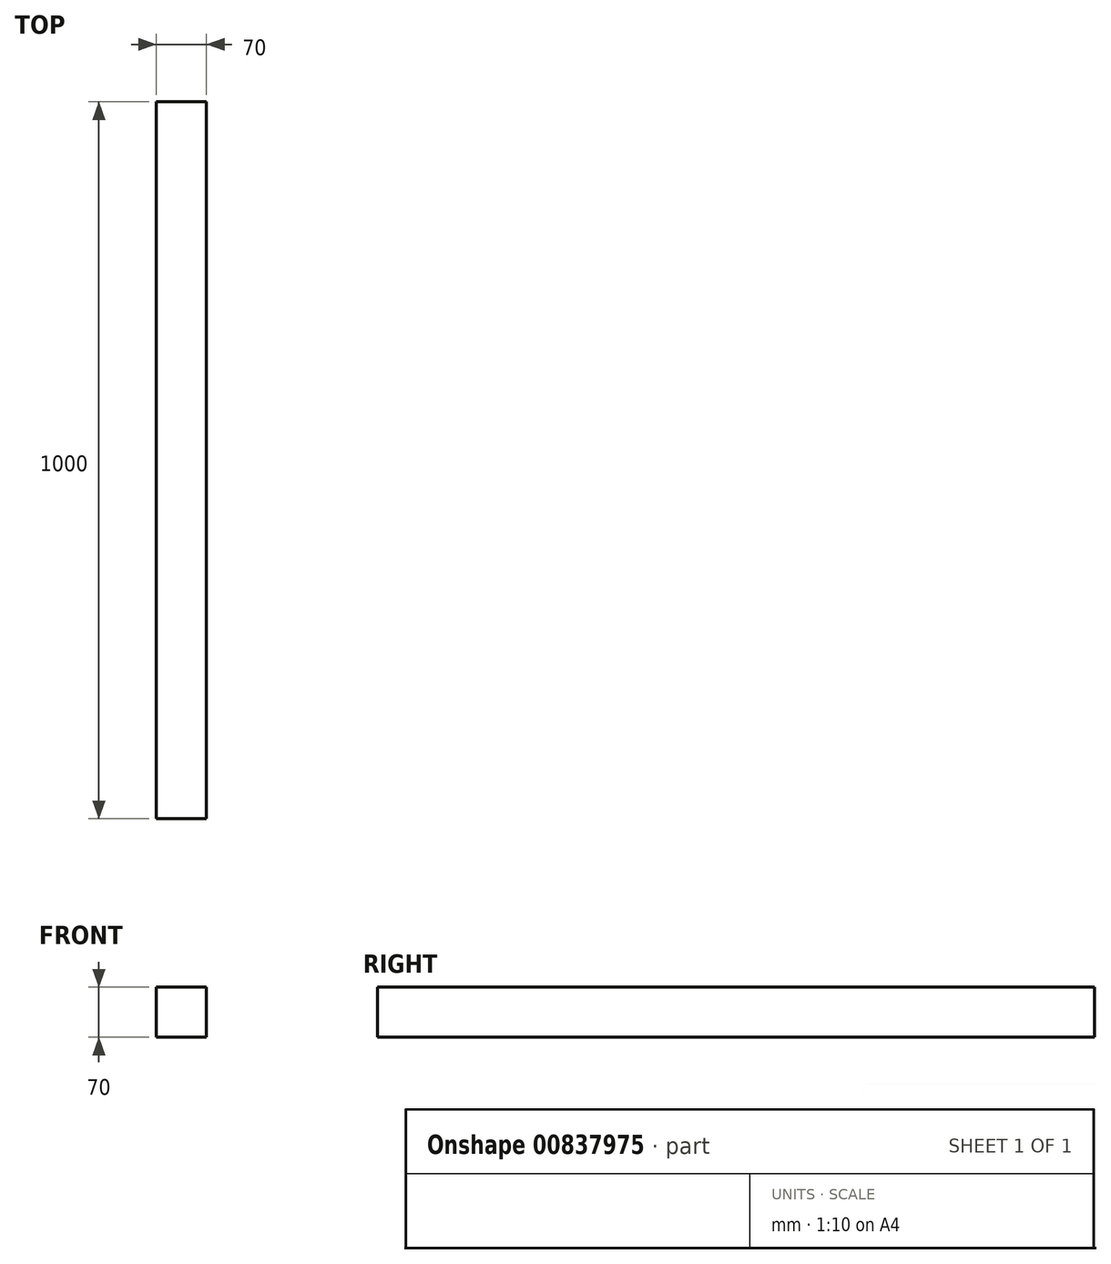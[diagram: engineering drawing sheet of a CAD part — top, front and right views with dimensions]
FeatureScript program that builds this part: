
annotation { "Feature Type Name" : "Feature", "Feature Type Description" : "" }
export const myFeature = defineFeature(function(context is Context, id is Id, definition is map)
    precondition{}
    {
        {
            var Q0;
            Q0=qCreatedBy(makeId("Front.planeOp"),FACE);
            var sketch = newSketch(context, id + "F0", { "sketchPlane" : qUnion([Q0])});
            skLineSegment(sketch, "E0.bottom", {"start": v(-32.67, 32.74) * mm, "end": v(37.33, 32.74) * mm});
            skLineSegment(sketch, "E0.top", {"start": v(-32.67, -37.26) * mm, "end": v(37.33, -37.26) * mm});
            skLineSegment(sketch, "E0.left", {"start": v(-32.67, 32.74) * mm, "end": v(-32.67, -37.26) * mm});
            skLineSegment(sketch, "E0.right", {"start": v(37.33, 32.74) * mm, "end": v(37.33, -37.26) * mm});
            skSolve(sketch);
        }
        {
            var Q0;
            Q0=makeQuery(id+"F0.imprint","IMPRINT",FACE,{"disambiguationData":[TD([[makeQuery(id+"F0.imprint","IMPRINT",EDGE,{"derivedFrom":sQuery(id+"F0.wireOp",EDGE,"E0.bottom")}),-1.0]])]});
            extrude(context, id + "F1", {"entities" : qUnion([Q0]), "depth" : 1000 * mm, "offsetDistance" : 25 * mm});
        }
    });
